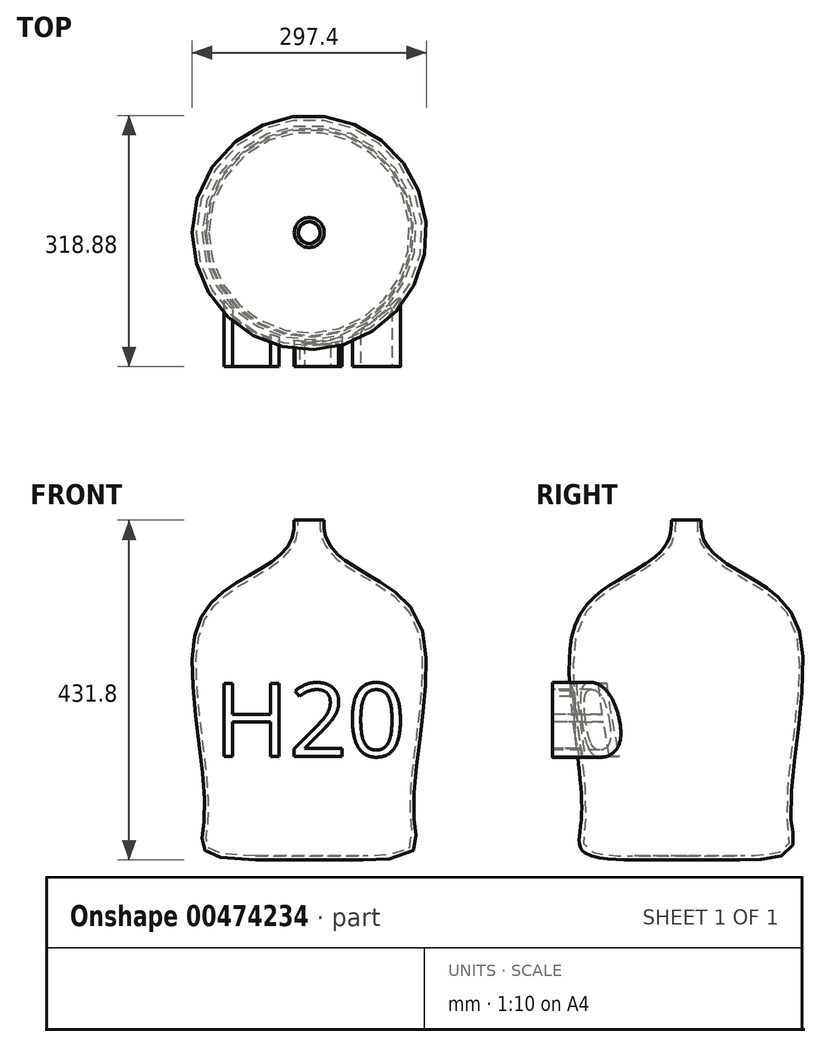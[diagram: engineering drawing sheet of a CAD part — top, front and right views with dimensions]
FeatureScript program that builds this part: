
annotation { "Feature Type Name" : "Feature", "Feature Type Description" : "" }
export const myFeature = defineFeature(function(context is Context, id is Id, definition is map)
    precondition{}
    {
        {
            var Q0;
            Q0=qCreatedBy(makeId("Front.planeOp"),FACE);
            var sketch = newSketch(context, id + "F0", { "sketchPlane" : qUnion([Q0])});
            skLineSegment(sketch, "E0", {"start": v(0, 0) * mm, "end": v(-68.46, 0) * mm});
            skFitSpline(sketch, "E1", {"points": [v(-68.46, 0) * mm, v(-133.16, 52.94) * mm, v(-144.93, 286.28) * mm, v(-86.12, 355.83) * mm, v(-38.2, 386.24) * mm, v(-20.17, 413.77) * mm, v(-19.4, 437.27) * mm], "startDerivative": vector(-1416.1, 0) * mm, "endDerivative": vector(-11, 176.23) * mm});
            skLineSegment(sketch, "E2", {"start": v(0, 0) * mm, "end": v(0, 431.8) * mm});
            skLineSegment(sketch, "E3", {"start": v(0, 431.8) * mm, "end": v(-19.05, 431.8) * mm});
            skSolve(sketch);
        }
        {
            var Q0;
            {var subQ1=sQuery(id+"F0.wireOp",EDGE,"E0");Q0=makeQuery(id+"F0.imprint","IMPRINT",FACE,{"disambiguationData":[TD([[makeQuery(id+"F0.imprint","IMPRINT",EDGE,{"derivedFrom":subQ1}),-1.0]])]});}
            var Q1;
            Q1=sQuery(id+"F0.wireOp",EDGE,"E2");
            revolve(context, id + "F1", {"entities" : qUnion([Q0]), "axis" : qUnion([Q1]), "revolveType" : RevolveType.FULL});
        }
        {
            var Q0;
            Q0=makeQuery(id+"F1.opRevolve","SWEPT_FACE",FACE,{"disambiguationData":[OSD([sQuery(id+"F0.wireOp",EDGE,"E3")])]});
            shell(context, id + "F2", {"entities" : qUnion([Q0]), "thickness" : 5.08 * mm});
        }
        {
            var Q0;
            Q0=qCreatedBy(makeId("Front.planeOp"),FACE);
            cPlane(context, id + "F3", {"entities" : qUnion([Q0]), "cplaneType" : CPlaneType.OFFSET, "offset" : 170.18 * mm, "width" : 152.4 * mm, "height" : 152.4 * mm});
        }
        {
            var Q0;
            Q0=qCreatedBy(id+"F3.planeOp",FACE);
            var sketch = newSketch(context, id + "F4", { "sketchPlane" : qUnion([Q0])});
            skText(sketch, "E4", { "text": "H20", "fontName": "OpenSans-Regular.ttf"});
            const initialGuessF4  = {"E4": [-0.12097, 0.1318, 1, 0, 0.0931]};
            skSetInitialGuess(sketch, initialGuessF4);
            skSolve(sketch);
        }
        {
            var Q0;
            Q0 = qSketchRegion(id + "F4", true);
            var Q1;
            Q1=makeQuery(id+"F1.opRevolve","SWEPT_FACE",FACE,{"disambiguationData":[OSD([sQuery(id+"F0.wireOp",EDGE,"E1")])]});
            extrude(context, id + "F5", {"entities" : qUnion([Q0]), "operationType" : NewBodyOperationType.ADD, "endBound" : BoundingType.UP_TO_SURFACE, "oppositeDirection" : true, "endBoundEntityFace" : qUnion([Q1]), "depth" : 42.16 * mm});
        }
    });
